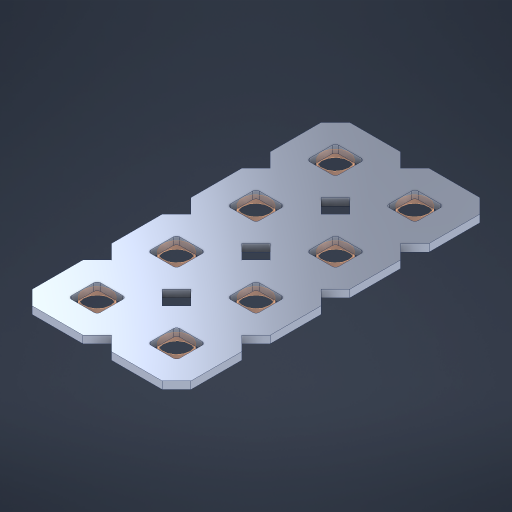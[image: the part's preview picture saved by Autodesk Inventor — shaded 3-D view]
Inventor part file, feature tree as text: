
AUTODESK INVENTOR PART (.ipt)
format: ipt  version: 2023 (Build 270158000, 158)  size: 336,896 bytes
history: native  units: in
note: dims shown in document units (in); Inventor stores cm internally (conversion verified against a paired STEP export)
features: other x9, extrude x7, sketch x2, pattern_linear x1
ambient origin geometry x8: Origin, YZ Plane, XZ Plane, XY Plane, X Axis, Y Axis, Z Axis, Center Point
bodies: Solid1 (feature_tree), Body (feature_tree)
feature tree (19):
  pattern_linear  "Rectangular Pattern1"  Spacing1=0.09in  [1 undecoded]
  sketch  "Sketch1"  dims[d1=0.5in]
  sketch  "Sketch2"  dims[d2=0.182in d3=0.09in d4=0.09in d5=0.09in d6=0.09in d7=0.09in d8=0.09in d9=0.09in d10=0.09in d11=0.02in d13=0.0in d14=0.172in d15=0.0625in d16=0.0in d19=0.5in d22=0.5in]
  other  "Srf1"
  other  "Srf126"
  other  "Srf127"
  other  "Srf128"
  other  "Srf268"
  other  "Srf269"
  other  "Srf270"
  other  "Srf271"
  other  "Circle"
  extrude  "ExtrusionSrf126"  Depth=0.09in
  extrude  "ExtrusionSrf127"  Depth=0.09in
  extrude  "ExtrusionSrf128"  Depth=0.09in
  extrude  "ExtrusionSrf268"  Depth=0.09in
  extrude  "ExtrusionSrf269"  Depth=0.09in
  extrude  "ExtrusionSrf270"  Depth=0.09in
  extrude  "ExtrusionSrf271"  Depth=0.09in
note: 1 required parameter value undecoded (feature->parameter linkage not recoverable at this tier; creation-order binding heuristic only, values carry confidence <= 0.55)
